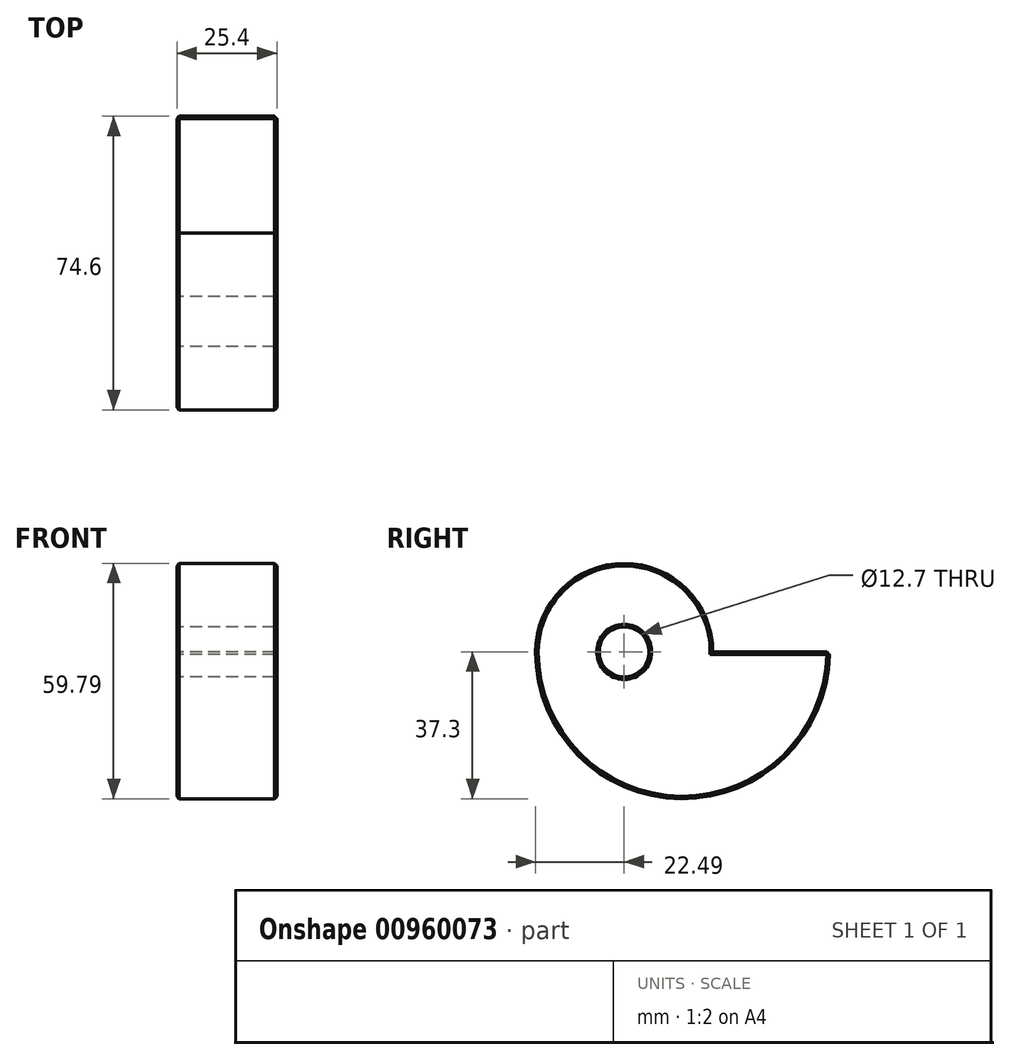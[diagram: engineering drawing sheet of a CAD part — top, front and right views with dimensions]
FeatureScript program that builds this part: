
annotation { "Feature Type Name" : "Feature", "Feature Type Description" : "" }
export const myFeature = defineFeature(function(context is Context, id is Id, definition is map)
    precondition{}
    {
        {
            var Q0;
            Q0=qCreatedBy(makeId("Right.planeOp"),FACE);
            var sketch = newSketch(context, id + "F0", { "sketchPlane" : qUnion([Q0])});
            skCircle(sketch, "E0", {"center": v(0, 0) * mm, "radius": 6.35 * mm});
            skArc(sketch, "E1", {"start": v(22.49, 0) * mm, "mid": v(0, 22.49) * mm, "end": v(-22.49, 0) * mm});
            skArc(sketch, "E2", {"start": v(-22.49, 0) * mm, "mid": v(14.81, -37.3) * mm, "end": v(52.12, 0) * mm});
            skLineSegment(sketch, "E3", {"start": v(52.12, 0) * mm, "end": v(52.12, 0) * mm});
            skLineSegment(sketch, "E4", {"start": v(22.49, 0) * mm, "end": v(52.12, 0) * mm});
            skSolve(sketch);
        }
        {
            var Q0;
            Q0 = qSketchRegion(id + "F0", true);
            extrude(context, id + "F1", {"entities" : qUnion([Q0]), "depth" : 25.4 * mm, "offsetDistance" : 25.4 * mm});
        }
        {
            var Q0;
            {var subQ0=sQuery(id+"F0.wireOp",EDGE,"eY8EP2Nv-zinG-kmOH-X74c-kDoCuLpC4Ygh.top");Q0=makeQuery(id+"FOGgPIscrUT7WdQ_2.opShell","OFFSET_EDGE",EDGE,{"disambiguationData":[OSD([subQ0]),TDD([makeQuery(id+"F1.opExtrude","CAP_EDGE",EDGE,{"disambiguationData":[OSD([subQ0])],"isStart":false})])]});}
            var Q1;
            {var subQ0=sQuery(id+"F0.wireOp",EDGE,"E1");Q1=makeQuery(id+"FOGgPIscrUT7WdQ_2.opShell","OFFSET_EDGE",EDGE,{"disambiguationData":[OSD([subQ0]),TDD([makeQuery(id+"F1.opExtrude","CAP_EDGE",EDGE,{"disambiguationData":[OSD([subQ0])],"isStart":false})])]});}
            var Q2;
            {var subQ0=sQuery(id+"F0.wireOp",EDGE,"E2");Q2=makeQuery(id+"FOGgPIscrUT7WdQ_2.opShell","OFFSET_EDGE",EDGE,{"disambiguationData":[OSD([subQ0]),TDD([makeQuery(id+"F1.opExtrude","CAP_EDGE",EDGE,{"disambiguationData":[OSD([subQ0])],"isStart":false})])]});}
            var Q3;
            Q3=makeQuery(id+"F1.opExtrude","CAP_EDGE",EDGE,{"disambiguationData":[OSD([sQuery(id+"F0.wireOp",EDGE,"E2")])],"isStart":false});
            var Q4;
            Q4=makeQuery(id+"F1.opExtrude","CAP_EDGE",EDGE,{"disambiguationData":[OSD([sQuery(id+"F0.wireOp",EDGE,"eY8EP2Nv-zinG-kmOH-X74c-kDoCuLpC4Ygh.top")])],"isStart":false});
            var Q5;
            Q5=makeQuery(id+"F1.opExtrude","CAP_EDGE",EDGE,{"disambiguationData":[OSD([sQuery(id+"F0.wireOp",EDGE,"E1")])],"isStart":false});
            var Q6;
            {var subQ0=sQuery(id+"F0.wireOp",EDGE,"E0");Q6=makeQuery(id+"FOGgPIscrUT7WdQ_2.opShell","OFFSET_EDGE",EDGE,{"disambiguationData":[OSD([subQ0]),TDD([makeQuery(id+"F1.opExtrude","CAP_EDGE",EDGE,{"disambiguationData":[OSD([subQ0])],"isStart":false})])]});}
            var Q7;
            Q7=makeQuery(id+"F1.opExtrude","CAP_EDGE",EDGE,{"disambiguationData":[OSD([sQuery(id+"F0.wireOp",EDGE,"E0")])],"isStart":false});
            chamfer(context, id + "F2", {"entities" : qUnion([Q0, Q1, Q2, Q3, Q4, Q5, Q6, Q7]), "width" : 0.64 * mm, "tangentPropagation" : true});
        }
        {
            var Q0;
            Q0=makeQuery(id+"F1.opExtrude","CAP_EDGE",EDGE,{"disambiguationData":[OSD([sQuery(id+"F0.wireOp",EDGE,"E0")])],"isStart":true});
            var Q1;
            Q1=makeQuery(id+"F1.opExtrude","CAP_EDGE",EDGE,{"disambiguationData":[OSD([sQuery(id+"F0.wireOp",EDGE,"E1")])],"isStart":true});
            var Q2;
            Q2=makeQuery(id+"F1.opExtrude","SWEPT_EDGE",EDGE,{"disambiguationData":[OSD([sQuery(id+"F0.wireOp",EDGE,"E2"),sQuery(id+"F0.wireOp",EDGE,"E4")])]});
            var Q3;
            Q3=makeQuery(id+"F1.opExtrude","CAP_EDGE",EDGE,{"disambiguationData":[OSD([sQuery(id+"F0.wireOp",EDGE,"E4")])],"isStart":true});
            var Q4;
            Q4=makeQuery(id+"F1.opExtrude","CAP_EDGE",EDGE,{"disambiguationData":[OSD([sQuery(id+"F0.wireOp",EDGE,"E4")])],"isStart":false});
            chamfer(context, id + "F3", {"entities" : qUnion([Q0, Q1, Q2, Q3, Q4]), "width" : 0.64 * mm, "tangentPropagation" : true});
        }
    });
